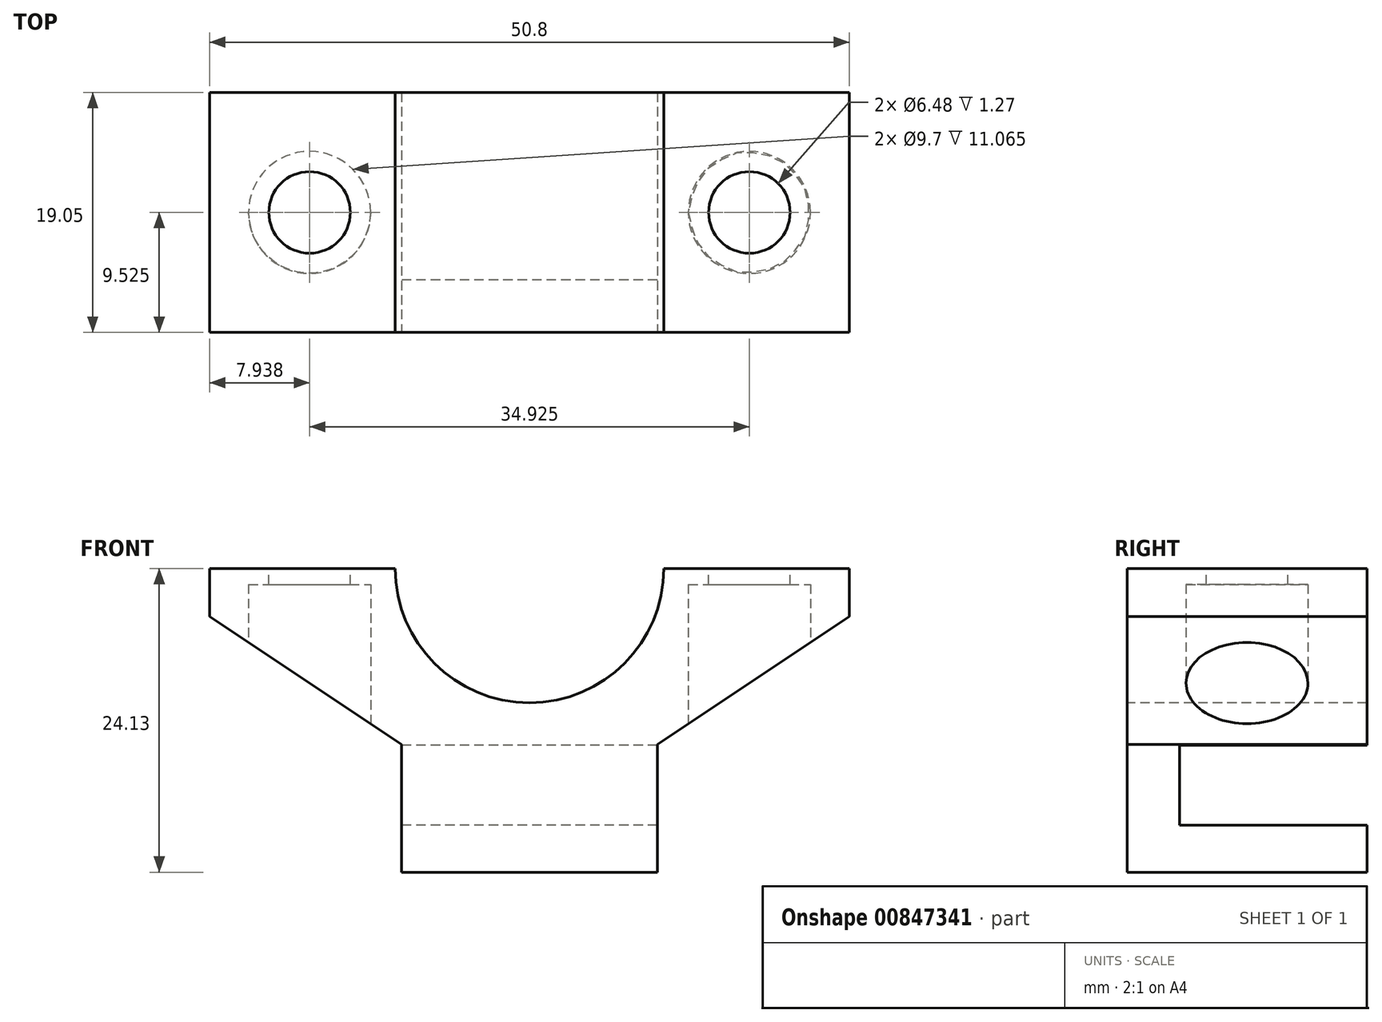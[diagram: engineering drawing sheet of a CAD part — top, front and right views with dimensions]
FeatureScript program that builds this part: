
annotation { "Feature Type Name" : "Feature", "Feature Type Description" : "" }
export const myFeature = defineFeature(function(context is Context, id is Id, definition is map)
    precondition{}
    {
        {
            var Q0;
            Q0=qCreatedBy(makeId("Front.planeOp"),FACE);
            var sketch = newSketch(context, id + "F0", { "sketchPlane" : qUnion([Q0])});
            skLineSegment(sketch, "E0.bottom", {"start": v(25.4, -13.97) * mm, "end": v(-25.4, -13.97) * mm});
            skLineSegment(sketch, "E0.top", {"start": v(25.4, 0) * mm, "end": v(-25.4, 0) * mm});
            skLineSegment(sketch, "E0.left", {"start": v(25.4, -13.97) * mm, "end": v(25.4, 0) * mm});
            skLineSegment(sketch, "E0.right", {"start": v(-25.4, -13.97) * mm, "end": v(-25.4, 0) * mm});
            skPoint(sketch, "E0.middle", {"position": v(-35.35, 0) * mm});
            skPoint(sketch, "E1", {"position": v(0, 0) * mm});
            skSolve(sketch);
        }
        {
            var Q0;
            Q0 = qSketchRegion(id + "F0", true);
            extrude(context, id + "F1", {"entities" : qUnion([Q0]), "oppositeDirection" : true, "depth" : 19.05 * mm, "offsetDistance" : 25.4 * mm});
        }
        {
            var Q0;
            Q0=makeQuery(id+"F0.imprint","IMPRINT",FACE,{"disambiguationData":[TD([[makeQuery(id+"F0.imprint","IMPRINT",EDGE,{"derivedFrom":sQuery(id+"F0.wireOp",EDGE,"E0.bottom")}),-1.0]])]});
            var sketch = newSketch(context, id + "F2", { "sketchPlane" : qUnion([Q0])});
            skCircle(sketch, "E2", {"center": v(0, 0) * mm, "radius": 10.67 * mm});
            skSolve(sketch);
        }
        {
            var Q0;
            {var subQ0=sQuery(id+"F2.wireOp",EDGE,"E2");var subQ1=makeQuery(id+"F0.imprint","IMPRINT",EDGE,{"derivedFrom":sQuery(id+"F0.wireOp",EDGE,"E0.top")});var subQ2=makeQuery(id+"F2.imprint","INTERSECT",VERTEX,{"disambiguationData":[OD(0.0)],"derivedFrom":[subQ1,subQ0]});Q0=makeQuery(id+"F2.imprint","IMPRINT",FACE,{"disambiguationData":[TD([[makeQuery(id+"F2.imprint","IMPRINT",EDGE,{"disambiguationData":[TD([[subQ2,1.0]])],"derivedFrom":subQ0}),1.0]])]});}
            var Q1;
            Q1=sQuery(id+"F2.wireOp",EDGE,"E2");
            extrude(context, id + "F3", {"entities" : qUnion([Q0]), "operationType" : NewBodyOperationType.REMOVE, "surfaceEntities" : qUnion([Q1]), "oppositeDirection" : true, "depth" : 19.05 * mm, "offsetDistance" : 25.4 * mm});
        }
        {
            var Q0;
            Q0=makeQuery(id+"F1.opExtrude","CAP_FACE",FACE,{"disambiguationData":[OSD([sQuery(id+"F0.wireOp",EDGE,"E0.bottom"),sQuery(id+"F0.wireOp",EDGE,"E0.top"),sQuery(id+"F0.wireOp",EDGE,"E0.left"),sQuery(id+"F0.wireOp",EDGE,"E0.right")])],"isStart":true});
            var sketch = newSketch(context, id + "F4", { "sketchPlane" : qUnion([Q0])});
            skLineSegment(sketch, "E3", {"start": v(-25.4, -13.97) * mm, "end": v(-25.4, -3.81) * mm});
            skLineSegment(sketch, "E4", {"start": v(-25.4, -3.81) * mm, "end": v(-10.16, -13.97) * mm});
            skLineSegment(sketch, "E5", {"start": v(-10.16, -13.97) * mm, "end": v(-25.4, -13.97) * mm});
            skLineSegment(sketch, "E6.MirrorCS", {"start": v(25.4, -3.81) * mm, "end": v(10.16, -13.97) * mm});
            skLineSegment(sketch, "E7.MirrorCS", {"start": v(10.16, -13.97) * mm, "end": v(25.4, -13.97) * mm});
            skLineSegment(sketch, "E8.MirrorCS", {"start": v(25.4, -13.97) * mm, "end": v(25.4, -3.81) * mm});
            skSolve(sketch);
        }
        {
            var Q0;
            Q0 = qSketchRegion(id + "F4", true);
            extrude(context, id + "F5", {"entities" : qUnion([Q0]), "operationType" : NewBodyOperationType.REMOVE, "oppositeDirection" : true, "depth" : 25.4 * mm, "offsetDistance" : 25.4 * mm});
        }
        {
            var Q0;
            {var subQ0=sQuery(id+"F0.wireOp",EDGE,"E0.right");var subQ2=sQuery(id+"F0.wireOp",EDGE,"E0.top");Q0=makeQuery(id+"F3.boolean.opBoolean","SPLIT",FACE,{"disambiguationData":[TD([makeQuery(id+"F1.opExtrude","SWEPT_FACE",FACE,{"disambiguationData":[OSD([subQ0])]})])],"derivedFrom":makeQuery(id+"F1.opExtrude","SWEPT_FACE",FACE,{"disambiguationData":[OSD([subQ2])]})});}
            var sketch = newSketch(context, id + "F6", { "sketchPlane" : qUnion([Q0])});
            skCircle(sketch, "E9", {"center": v(-17.46, 9.52) * mm, "radius": 3.24 * mm});
            skCircle(sketch, "E10.MirrorC", {"center": v(17.46, 9.52) * mm, "radius": 3.24 * mm});
            skSolve(sketch);
        }
        {
            var Q0;
            Q0 = qSketchRegion(id + "F6", true);
            extrude(context, id + "F7", {"entities" : qUnion([Q0]), "operationType" : NewBodyOperationType.REMOVE, "oppositeDirection" : true, "depth" : 25.4 * mm, "offsetDistance" : 25.4 * mm});
        }
        {
            var Q0;
            Q0=makeQuery(id+"F1.opExtrude","SWEPT_FACE",FACE,{"disambiguationData":[OSD([sQuery(id+"F0.wireOp",EDGE,"E0.bottom")])]});
            var sketch = newSketch(context, id + "F8", { "sketchPlane" : qUnion([Q0])});
            skCircle(sketch, "E11", {"center": v(-17.46, -9.52) * mm, "radius": 4.85 * mm});
            skCircle(sketch, "E12.MirrorC", {"center": v(17.46, -9.52) * mm, "radius": 4.85 * mm});
            skSolve(sketch);
        }
        {
            var Q0;
            Q0 = qSketchRegion(id + "F8", true);
            extrude(context, id + "F9", {"entities" : qUnion([Q0]), "operationType" : NewBodyOperationType.REMOVE, "oppositeDirection" : true, "depth" : 12.7 * mm, "offsetDistance" : 25.4 * mm});
        }
        {
            var Q0;
            Q0=makeQuery(id+"F1.opExtrude","SWEPT_FACE",FACE,{"disambiguationData":[OSD([sQuery(id+"F0.wireOp",EDGE,"E0.bottom")])]});
            var sketch = newSketch(context, id + "F10", { "sketchPlane" : qUnion([Q0])});
            skLineSegment(sketch, "E13.bottom", {"start": v(-10.16, 0) * mm, "end": v(10.16, 0) * mm});
            skLineSegment(sketch, "E13.top", {"start": v(-10.16, -19.05) * mm, "end": v(10.16, -19.05) * mm});
            skLineSegment(sketch, "E13.left", {"start": v(-10.16, 0) * mm, "end": v(-10.16, -19.05) * mm});
            skLineSegment(sketch, "E13.right", {"start": v(10.16, 0) * mm, "end": v(10.16, -19.05) * mm});
            skSolve(sketch);
        }
        {
            var Q0;
            Q0 = qSketchRegion(id + "F10", true);
            extrude(context, id + "F11", {"entities" : qUnion([Q0]), "operationType" : NewBodyOperationType.ADD, "depth" : 10.16 * mm, "offsetDistance" : 25.4 * mm});
        }
        {
            var Q0;
            Q0=makeQuery(id+"F11.opExtrude","SWEPT_FACE",FACE,{"disambiguationData":[OSD([sQuery(id+"F10.wireOp",EDGE,"E13.left")])]});
            var sketch = newSketch(context, id + "F12", { "sketchPlane" : qUnion([Q0])});
            skLineSegment(sketch, "E14.bottom", {"start": v(-19.05, -14.03) * mm, "end": v(-4.16, -14.03) * mm});
            skLineSegment(sketch, "E14.top", {"start": v(-19.05, -20.38) * mm, "end": v(-4.16, -20.38) * mm});
            skLineSegment(sketch, "E14.left", {"start": v(-19.05, -14.03) * mm, "end": v(-19.05, -20.38) * mm});
            skLineSegment(sketch, "E14.right", {"start": v(-4.16, -14.03) * mm, "end": v(-4.16, -20.38) * mm});
            skSolve(sketch);
        }
        {
            var Q0;
            Q0 = qSketchRegion(id + "F12", true);
            extrude(context, id + "F13", {"entities" : qUnion([Q0]), "operationType" : NewBodyOperationType.REMOVE, "oppositeDirection" : true, "depth" : 25.4 * mm, "offsetDistance" : 25.4 * mm});
        }
    });
